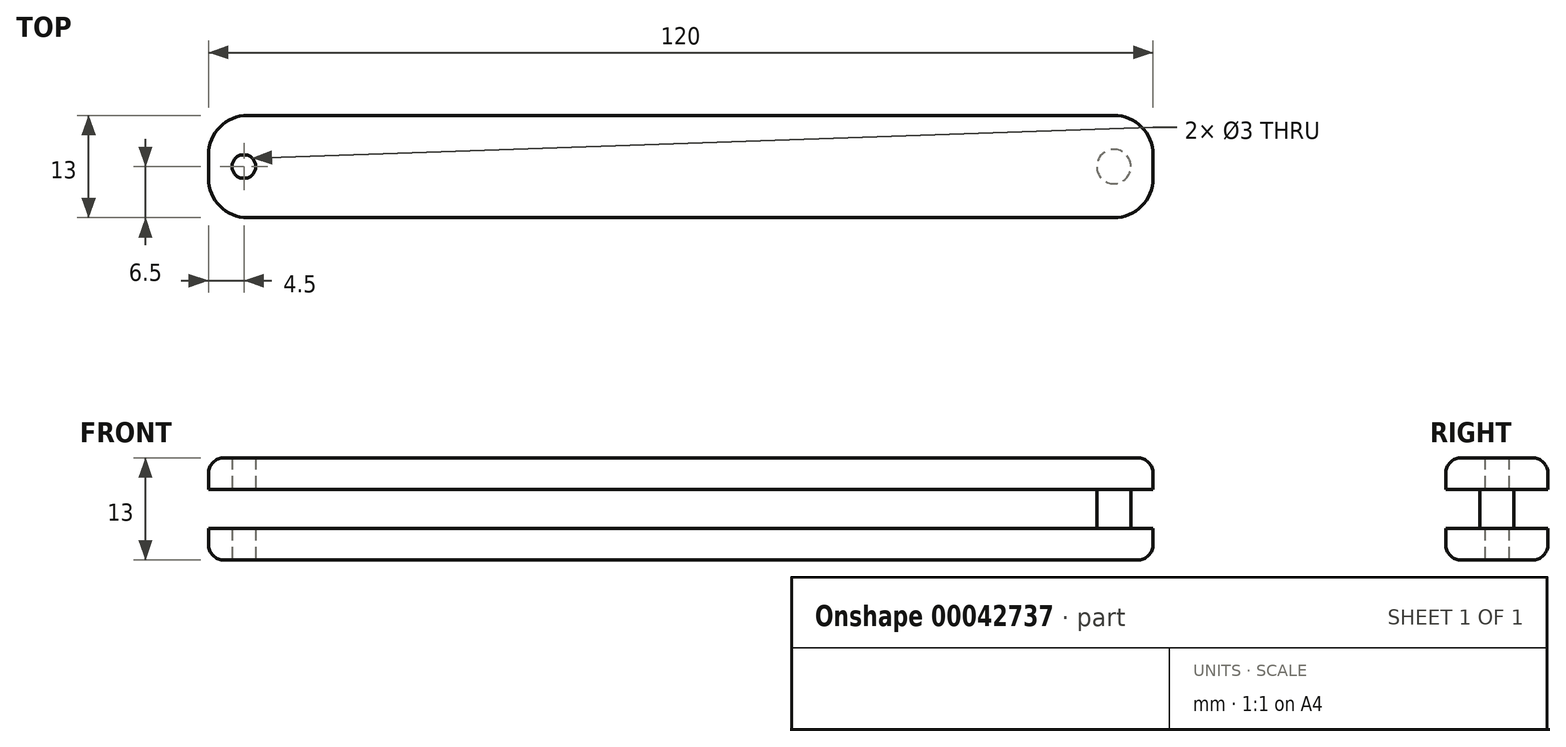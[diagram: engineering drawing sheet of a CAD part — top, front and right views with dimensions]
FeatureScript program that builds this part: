
annotation { "Feature Type Name" : "Feature", "Feature Type Description" : "" }
export const myFeature = defineFeature(function(context is Context, id is Id, definition is map)
    precondition{}
    {
        {
            var Q0;
            Q0=qCreatedBy(makeId("Top.planeOp"),FACE);
            var sketch = newSketch(context, id + "F0", { "sketchPlane" : qUnion([Q0])});
            skLineSegment(sketch, "E0.rect.bottom", {"start": v(60, 6.5) * mm, "end": v(-60, 6.5) * mm});
            skLineSegment(sketch, "E0.rect.top", {"start": v(60, -6.5) * mm, "end": v(-60, -6.5) * mm});
            skLineSegment(sketch, "E0.rect.left", {"start": v(60, 6.5) * mm, "end": v(60, -6.5) * mm});
            skLineSegment(sketch, "E0.rect.right", {"start": v(-60, 6.5) * mm, "end": v(-60, -6.5) * mm});
            skPoint(sketch, "E0.rect.middle", {"position": v(0, 0) * mm});
            skLineSegment(sketch, "E1", {"start": v(0, 6.5) * mm, "end": v(0, -6.5) * mm, "construction": true});
            skLineSegment(sketch, "E2", {"start": v(-60, 0) * mm, "end": v(60, 0) * mm, "construction": true});
            skLineSegment(sketch, "E3", {"start": v(-60, 0) * mm, "end": v(-55.5, 0) * mm, "construction": true});
            skCircle(sketch, "E4", {"center": v(-55.5, 0) * mm, "radius": 1.5 * mm});
            skLineSegment(sketch, "E5", {"start": v(60, 0) * mm, "end": v(55, 0) * mm, "construction": true});
            skSolve(sketch);
        }
        {
            var Q0;
            Q0 = qSketchRegion(id + "F0", true);
            extrude(context, id + "F1", {"entities" : qUnion([Q0]), "depth" : 13 * mm});
        }
        {
            var Q0;
            Q0=qCreatedBy(makeId("Front.planeOp"),FACE);
            var sketch = newSketch(context, id + "F2", { "sketchPlane" : qUnion([Q0])});
            skLineSegment(sketch, "E6", {"start": v(0, 0) * mm, "end": v(0, 13) * mm, "construction": true});
            skLineSegment(sketch, "E7.rect.bottom", {"start": v(60, 9) * mm, "end": v(-60, 9) * mm});
            skLineSegment(sketch, "E7.rect.top", {"start": v(60, 4) * mm, "end": v(-60, 4) * mm});
            skLineSegment(sketch, "E7.rect.left", {"start": v(60, 9) * mm, "end": v(60, 4) * mm});
            skLineSegment(sketch, "E7.rect.right", {"start": v(-60, 9) * mm, "end": v(-60, 4) * mm});
            skPoint(sketch, "E7.rect.middle", {"position": v(0, 6.5) * mm});
            skSolve(sketch);
        }
        {
            var Q0;
            Q0=makeQuery(id+"F2.imprint","IMPRINT",FACE,{"disambiguationData":[TD([[makeQuery(id+"F2.imprint","IMPRINT",EDGE,{"derivedFrom":sQuery(id+"F2.wireOp",EDGE,"E7.rect.bottom")}),1.0]])]});
            extrude(context, id + "F3", {"entities" : qUnion([Q0]), "operationType" : NewBodyOperationType.REMOVE, "oppositeDirection" : true, "depth" : 8 * mm, "hasSecondDirection" : true, "secondDirectionOppositeDirection" : false, "secondDirectionDepth" : 8 * mm});
        }
        {
            var Q0;
            Q0=qCreatedBy(makeId("Top.planeOp"),FACE);
            var sketch = newSketch(context, id + "F4", { "sketchPlane" : qUnion([Q0])});
            skCircle(sketch, "E8", {"center": v(55.01, 0) * mm, "radius": 2.17 * mm});
            skSolve(sketch);
        }
        {
            var Q0;
            Q0 = qSketchRegion(id + "F4", true);
            extrude(context, id + "F5", {"entities" : qUnion([Q0]), "operationType" : NewBodyOperationType.ADD, "depth" : 13 * mm});
        }
        {
            var Q0;
            Q0=makeQuery(id+"F1.opExtrude","CAP_EDGE",EDGE,{"disambiguationData":[OSD([sQuery(id+"F0.wireOp",EDGE,"E0.rect.top")])],"isStart":false});
            var Q1;
            Q1=makeQuery(id+"F1.opExtrude","CAP_EDGE",EDGE,{"disambiguationData":[OSD([sQuery(id+"F0.wireOp",EDGE,"E0.rect.right")])],"isStart":false});
            var Q2;
            Q2=makeQuery(id+"F1.opExtrude","CAP_EDGE",EDGE,{"disambiguationData":[OSD([sQuery(id+"F0.wireOp",EDGE,"E0.rect.bottom")])],"isStart":false});
            var Q3;
            Q3=makeQuery(id+"F1.opExtrude","CAP_EDGE",EDGE,{"disambiguationData":[OSD([sQuery(id+"F0.wireOp",EDGE,"E0.rect.left")])],"isStart":false});
            var Q4;
            Q4=makeQuery(id+"F1.opExtrude","CAP_EDGE",EDGE,{"disambiguationData":[OSD([sQuery(id+"F0.wireOp",EDGE,"E0.rect.right")])],"isStart":true});
            var Q5;
            Q5=makeQuery(id+"F1.opExtrude","CAP_EDGE",EDGE,{"disambiguationData":[OSD([sQuery(id+"F0.wireOp",EDGE,"E0.rect.top")])],"isStart":true});
            var Q6;
            Q6=makeQuery(id+"F1.opExtrude","CAP_EDGE",EDGE,{"disambiguationData":[OSD([sQuery(id+"F0.wireOp",EDGE,"E0.rect.left")])],"isStart":true});
            var Q7;
            Q7=makeQuery(id+"F1.opExtrude","CAP_EDGE",EDGE,{"disambiguationData":[OSD([sQuery(id+"F0.wireOp",EDGE,"E0.rect.bottom")])],"isStart":true});
            fillet(context, id + "F6", {"entities" : qUnion([Q0, Q1, Q2, Q3, Q4, Q5, Q6, Q7]), "radius" : 2 * mm, "tangentPropagation" : true, "allowEdgeOverflow" : false});
        }
        {
            var Q0;
            {var subQ0=sQuery(id+"F0.wireOp",EDGE,"E0.rect.top");var subQ1=sQuery(id+"F0.wireOp",EDGE,"E0.rect.right");Q0=makeQuery(id+"F3.boolean.opBoolean","SPLIT",EDGE,{"disambiguationData":[TD([makeQuery(id+"F3.opExtrude","SWEPT_FACE",FACE,{"disambiguationData":[OSD([sQuery(id+"F2.wireOp",EDGE,"E7.rect.bottom")])]})])],"derivedFrom":makeQuery(id+"F1.opExtrude","SWEPT_EDGE",EDGE,{"disambiguationData":[OSD([subQ0,subQ1])]})});}
            var Q1;
            {var subQ0=sQuery(id+"F0.wireOp",EDGE,"E0.rect.bottom");var subQ1=sQuery(id+"F0.wireOp",EDGE,"E0.rect.right");Q1=makeQuery(id+"F3.boolean.opBoolean","SPLIT",EDGE,{"disambiguationData":[TD([makeQuery(id+"F3.opExtrude","SWEPT_FACE",FACE,{"disambiguationData":[OSD([sQuery(id+"F2.wireOp",EDGE,"E7.rect.bottom")])]})])],"derivedFrom":makeQuery(id+"F1.opExtrude","SWEPT_EDGE",EDGE,{"disambiguationData":[OSD([subQ0,subQ1])]})});}
            var Q2;
            {var subQ0=sQuery(id+"F0.wireOp",EDGE,"E0.rect.top");var subQ1=sQuery(id+"F0.wireOp",EDGE,"E0.rect.right");Q2=makeQuery(id+"F3.boolean.opBoolean","SPLIT",EDGE,{"disambiguationData":[TD([makeQuery(id+"F3.opExtrude","SWEPT_FACE",FACE,{"disambiguationData":[OSD([sQuery(id+"F2.wireOp",EDGE,"E7.rect.top")])]})])],"derivedFrom":makeQuery(id+"F1.opExtrude","SWEPT_EDGE",EDGE,{"disambiguationData":[OSD([subQ0,subQ1])]})});}
            var Q3;
            {var subQ0=sQuery(id+"F0.wireOp",EDGE,"E0.rect.bottom");var subQ1=sQuery(id+"F0.wireOp",EDGE,"E0.rect.right");Q3=makeQuery(id+"F3.boolean.opBoolean","SPLIT",EDGE,{"disambiguationData":[TD([makeQuery(id+"F3.opExtrude","SWEPT_FACE",FACE,{"disambiguationData":[OSD([sQuery(id+"F2.wireOp",EDGE,"E7.rect.top")])]})])],"derivedFrom":makeQuery(id+"F1.opExtrude","SWEPT_EDGE",EDGE,{"disambiguationData":[OSD([subQ0,subQ1])]})});}
            var Q4;
            {var subQ0=sQuery(id+"F0.wireOp",EDGE,"E0.rect.top");var subQ1=sQuery(id+"F0.wireOp",EDGE,"E0.rect.left");Q4=makeQuery(id+"F3.boolean.opBoolean","SPLIT",EDGE,{"disambiguationData":[TD([makeQuery(id+"F3.opExtrude","SWEPT_FACE",FACE,{"disambiguationData":[OSD([sQuery(id+"F2.wireOp",EDGE,"E7.rect.bottom")])]})])],"derivedFrom":makeQuery(id+"F1.opExtrude","SWEPT_EDGE",EDGE,{"disambiguationData":[OSD([subQ0,subQ1])]})});}
            var Q5;
            {var subQ0=sQuery(id+"F0.wireOp",EDGE,"E0.rect.bottom");var subQ1=sQuery(id+"F0.wireOp",EDGE,"E0.rect.left");Q5=makeQuery(id+"F3.boolean.opBoolean","SPLIT",EDGE,{"disambiguationData":[TD([makeQuery(id+"F3.opExtrude","SWEPT_FACE",FACE,{"disambiguationData":[OSD([sQuery(id+"F2.wireOp",EDGE,"E7.rect.bottom")])]})])],"derivedFrom":makeQuery(id+"F1.opExtrude","SWEPT_EDGE",EDGE,{"disambiguationData":[OSD([subQ0,subQ1])]})});}
            var Q6;
            {var subQ0=sQuery(id+"F0.wireOp",EDGE,"E0.rect.top");var subQ1=sQuery(id+"F0.wireOp",EDGE,"E0.rect.left");Q6=makeQuery(id+"F3.boolean.opBoolean","SPLIT",EDGE,{"disambiguationData":[TD([makeQuery(id+"F3.opExtrude","SWEPT_FACE",FACE,{"disambiguationData":[OSD([sQuery(id+"F2.wireOp",EDGE,"E7.rect.top")])]})])],"derivedFrom":makeQuery(id+"F1.opExtrude","SWEPT_EDGE",EDGE,{"disambiguationData":[OSD([subQ0,subQ1])]})});}
            var Q7;
            {var subQ0=sQuery(id+"F0.wireOp",EDGE,"E0.rect.bottom");var subQ1=sQuery(id+"F0.wireOp",EDGE,"E0.rect.left");Q7=makeQuery(id+"F3.boolean.opBoolean","SPLIT",EDGE,{"disambiguationData":[TD([makeQuery(id+"F3.opExtrude","SWEPT_FACE",FACE,{"disambiguationData":[OSD([sQuery(id+"F2.wireOp",EDGE,"E7.rect.top")])]})])],"derivedFrom":makeQuery(id+"F1.opExtrude","SWEPT_EDGE",EDGE,{"disambiguationData":[OSD([subQ0,subQ1])]})});}
            fillet(context, id + "F7", {"entities" : qUnion([Q0, Q1, Q2, Q3, Q4, Q5, Q6, Q7]), "radius" : 5 * mm, "tangentPropagation" : true, "allowEdgeOverflow" : false});
        }
    });
